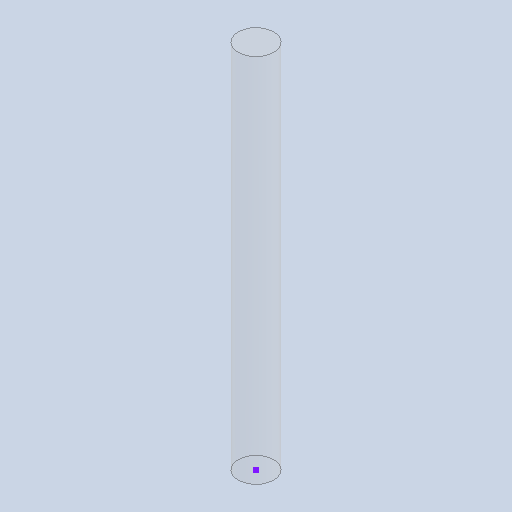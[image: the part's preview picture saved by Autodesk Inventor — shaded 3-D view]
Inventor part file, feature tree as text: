
AUTODESK INVENTOR PART (.ipt)
format: ipt  version: 2022.4 (Build 264492010, 492A)  size: 83,456 bytes
history: native  units: mm
features: other x1, sketch x1
ambient origin geometry x8: Origin, YZ Plane, XZ Plane, XY Plane, X Axis, Y Axis, Z Axis, Center Point
bodies: Solid2 (feature_tree), Solid1 (feature_tree)
feature tree (2):
  other  "Repaired Geometry1"
  sketch  "Sketch1"
